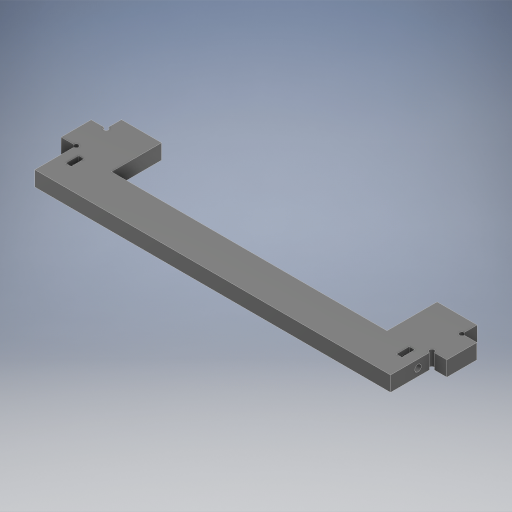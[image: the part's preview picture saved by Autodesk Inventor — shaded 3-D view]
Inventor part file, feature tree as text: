
AUTODESK INVENTOR PART (.ipt)
format: ipt  version: 2024 (Build 280153000, 153)  size: 373,760 bytes
history: native  units: in
note: dims shown in document units (in); Inventor stores cm internally (conversion verified against a paired STEP export)
features: extrude x7, other x7, sketch x7, reference x2, projected_geometry x2
ambient origin geometry x4: Origin, X Axis, Y Axis, Z Axis
bodies: Body1 (feature_tree)
feature tree (25):
  extrude  "돌출2"  Depth=5.5906in
  extrude  "돌출3"  Depth=1.937in
  extrude  "돌출4"  Depth=0.2362in
  extrude  "돌출5"  Depth=0.4724in
  extrude  "돌출6"  Depth=0.2362in
  extrude  "돌출8"  Depth=2.1654in
  extrude  "돌출9"  Depth=0.7874in
  other  "우측면도"
  other  "평면도"
  other  "정면도"
  sketch  "스케치1"
  sketch  "스케치2"
  sketch  "스케치3"
  reference  "참조1"
  sketch  "스케치4"
  reference  "참조2"
  sketch  "스케치5"
  sketch  "스케치6"
  projected_geometry  "투영된 루프1"
  sketch  "스케치7"
  projected_geometry  "투영된 루프2"
  other  "<userpath>\Desktop\ROBIT\probationary_member\inventor\fight\fight_robot.iam"
  other  "fight_robot.iam"
  other  "battery_conn:4"
  other  "battery_conn:3"
